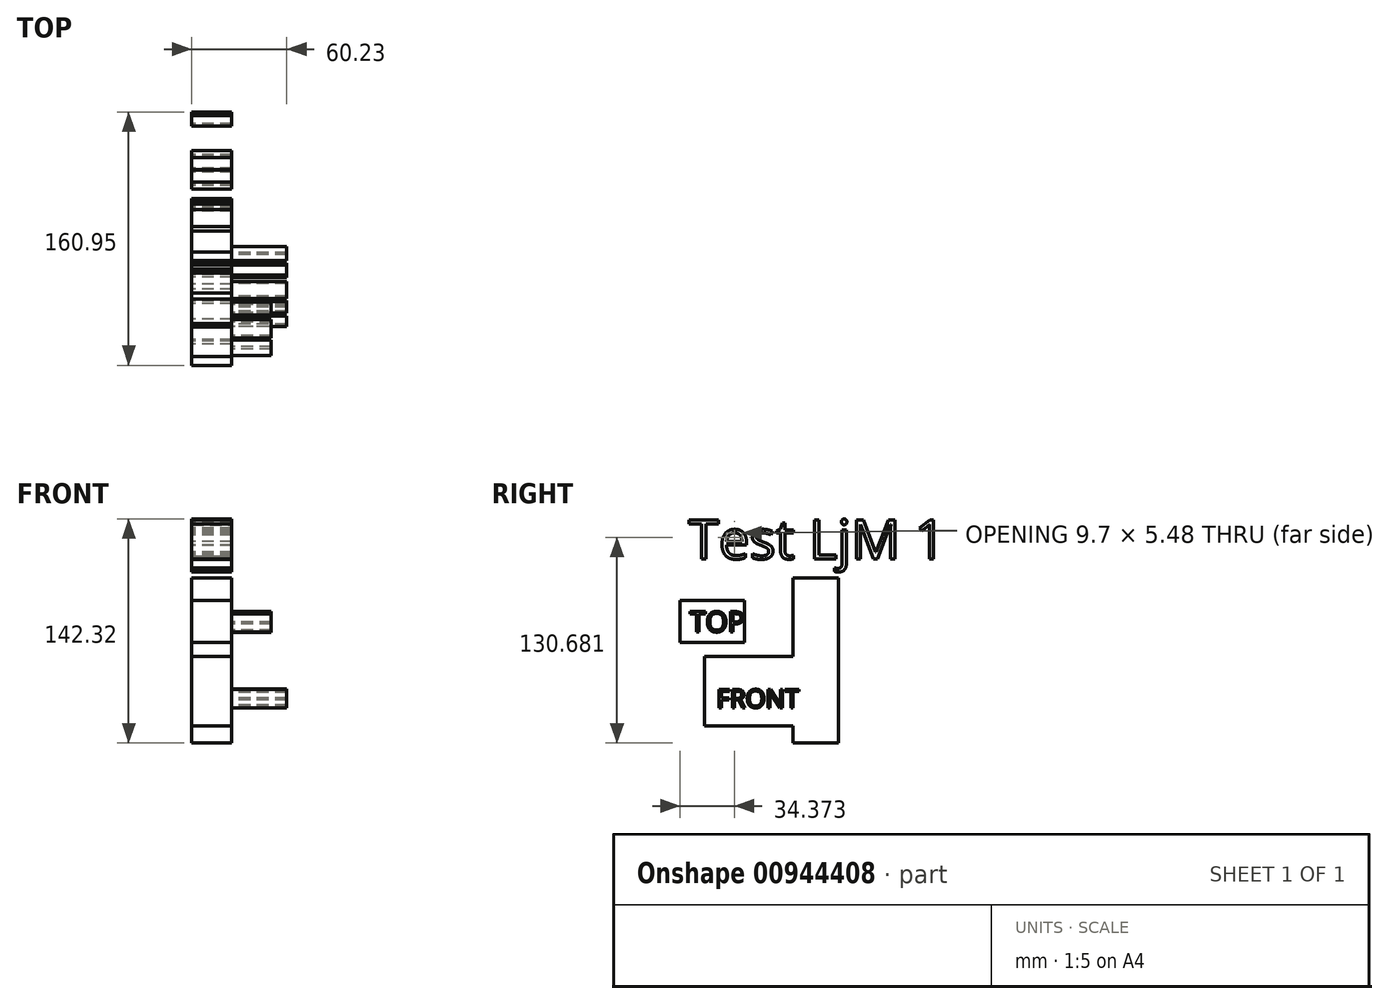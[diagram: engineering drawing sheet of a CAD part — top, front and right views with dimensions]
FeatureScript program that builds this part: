
annotation { "Feature Type Name" : "Feature", "Feature Type Description" : "" }
export const myFeature = defineFeature(function(context is Context, id is Id, definition is map)
    precondition{}
    {
        {
            var Q0;
            Q0=qCreatedBy(makeId("Right.planeOp"),FACE);
            var sketch = newSketch(context, id + "F0", { "sketchPlane" : qUnion([Q0])});
            skLineSegment(sketch, "E0.bottom", {"start": v(45.96, -44.31) * mm, "end": v(-25.55, -44.31) * mm});
            skLineSegment(sketch, "E0.top", {"start": v(45.96, 0) * mm, "end": v(-25.55, 0) * mm});
            skLineSegment(sketch, "E0.left", {"start": v(45.96, -44.31) * mm, "end": v(45.96, 0) * mm});
            skLineSegment(sketch, "E0.right", {"start": v(-25.55, -44.31) * mm, "end": v(-25.55, 0) * mm});
            skLineSegment(sketch, "E1.bottom", {"start": v(0, 8.67) * mm, "end": v(-41.03, 8.67) * mm});
            skLineSegment(sketch, "E1.top", {"start": v(0, 35.36) * mm, "end": v(-41.03, 35.36) * mm});
            skLineSegment(sketch, "E1.left", {"start": v(0, 8.67) * mm, "end": v(0, 35.36) * mm});
            skLineSegment(sketch, "E1.right", {"start": v(-41.03, 8.67) * mm, "end": v(-41.03, 35.36) * mm});
            skLineSegment(sketch, "E2.bottom", {"start": v(59.48, -55.08) * mm, "end": v(30.8, -55.08) * mm});
            skLineSegment(sketch, "E2.top", {"start": v(59.48, 49.83) * mm, "end": v(30.8, 49.83) * mm});
            skLineSegment(sketch, "E2.left", {"start": v(59.48, -55.08) * mm, "end": v(59.48, 49.83) * mm});
            skLineSegment(sketch, "E2.right", {"start": v(30.8, -55.08) * mm, "end": v(30.8, 49.83) * mm});
            skText(sketch, "E3", { "text": "Test LjM 1\n", "fontName": "OpenSans-Regular.ttf"});
            const initialGuessF0  = {"E3": [-0.0356, 0.06181, 1, 0, 0.02495]};
            skSetInitialGuess(sketch, initialGuessF0);
            skSolve(sketch);
        }
        {
            var Q0;
            Q0 = qSketchRegion(id + "F0", true);
            extrude(context, id + "F1", {"entities" : qUnion([Q0]), "depth" : 25.4 * mm, "offsetDistance" : 25.4 * mm});
        }
        {
            var Q0;
            Q0=makeQuery(id+"F1.opExtrude","CAP_FACE",FACE,{"disambiguationData":[OSD([sQuery(id+"F0.wireOp",EDGE,"E0.bottom"),sQuery(id+"F0.wireOp",EDGE,"E0.top"),sQuery(id+"F0.wireOp",EDGE,"E0.right"),sQuery(id+"F0.wireOp",EDGE,"E2.bottom"),sQuery(id+"F0.wireOp",EDGE,"E2.top"),sQuery(id+"F0.wireOp",EDGE,"E2.left"),sQuery(id+"F0.wireOp",EDGE,"E2.right")])],"isStart":false});
            var sketch = newSketch(context, id + "F2", { "sketchPlane" : qUnion([Q0])});
            skText(sketch, "E4", { "text": "FRONT", "fontName": "OpenSans-Regular.ttf"});
            const initialGuessF2  = {"E4": [-0.01784, -0.03268, 1, 0, 0.0117]};
            skSetInitialGuess(sketch, initialGuessF2);
            skSolve(sketch);
        }
        {
            var Q0;
            Q0 = qSketchRegion(id + "F2", true);
            extrude(context, id + "F3", {"entities" : qUnion([Q0]), "operationType" : NewBodyOperationType.ADD, "depth" : 34.83 * mm, "offsetDistance" : 25 * mm});
        }
        {
            var Q0;
            Q0=makeQuery(id+"F1.opExtrude","CAP_FACE",FACE,{"disambiguationData":[OSD([sQuery(id+"F0.wireOp",EDGE,"E1.bottom"),sQuery(id+"F0.wireOp",EDGE,"E1.top"),sQuery(id+"F0.wireOp",EDGE,"E1.left"),sQuery(id+"F0.wireOp",EDGE,"E1.right")])],"isStart":false});
            var sketch = newSketch(context, id + "F4", { "sketchPlane" : qUnion([Q0])});
            skText(sketch, "E5", { "text": "TOP", "fontName": "OpenSans-Regular.ttf"});
            const initialGuessF4  = {"E5": [-0.03486, 0.01544, 1, 0, 0.013]};
            skSetInitialGuess(sketch, initialGuessF4);
            skSolve(sketch);
        }
        {
            var Q0;
            Q0 = qSketchRegion(id + "F4", true);
            extrude(context, id + "F5", {"entities" : qUnion([Q0]), "operationType" : NewBodyOperationType.ADD, "depth" : 25 * mm, "offsetDistance" : 25 * mm});
        }
    });
